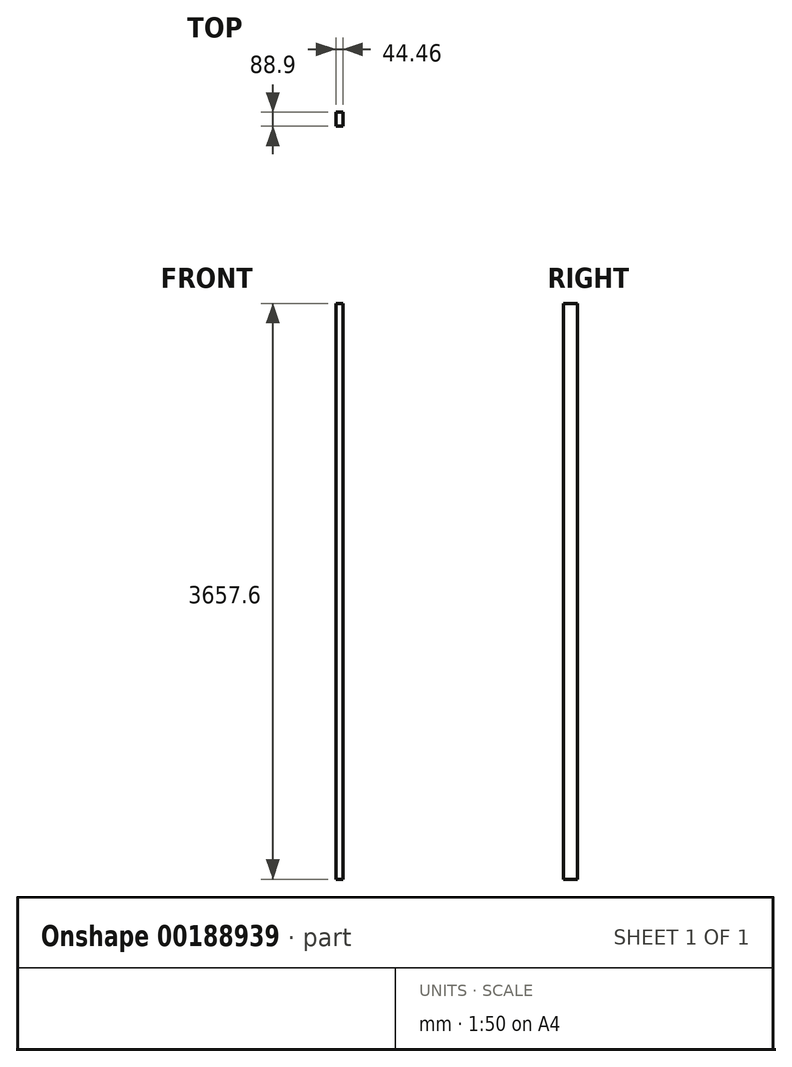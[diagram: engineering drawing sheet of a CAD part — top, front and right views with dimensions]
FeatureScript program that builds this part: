
annotation { "Feature Type Name" : "Feature", "Feature Type Description" : "" }
export const myFeature = defineFeature(function(context is Context, id is Id, definition is map)
    precondition{}
    {
        {
            var Q0;
            Q0=qCreatedBy(makeId("Top.planeOp"),FACE);
            var sketch = newSketch(context, id + "F1", { "sketchPlane" : qUnion([Q0])});
            skLineSegment(sketch, "E0.bottom", {"start": v(22.23, -44.45) * mm, "end": v(-22.22, -44.45) * mm});
            skLineSegment(sketch, "E0.top", {"start": v(22.22, 44.45) * mm, "end": v(-22.23, 44.45) * mm});
            skLineSegment(sketch, "E0.left", {"start": v(22.23, -44.45) * mm, "end": v(22.22, 44.45) * mm});
            skLineSegment(sketch, "E0.right", {"start": v(-22.22, -44.45) * mm, "end": v(-22.23, 44.45) * mm});
            skPoint(sketch, "E0.middle", {"position": v(0, 0) * mm});
            skSolve(sketch);
        }
        {
            var Q0;
            Q0=makeQuery(id+"F1.imprint","IMPRINT",FACE,{"disambiguationData":[TD([[makeQuery(id+"F1.imprint","IMPRINT",EDGE,{"derivedFrom":sQuery(id+"F1.wireOp",EDGE,"E0.bottom")}),-1.0]])]});
            extrude(context, id + "F0", {"entities" : qUnion([Q0]), "endBound" : BoundingType.SYMMETRIC, "depth" : 3657.6 * mm});
        }
    });
